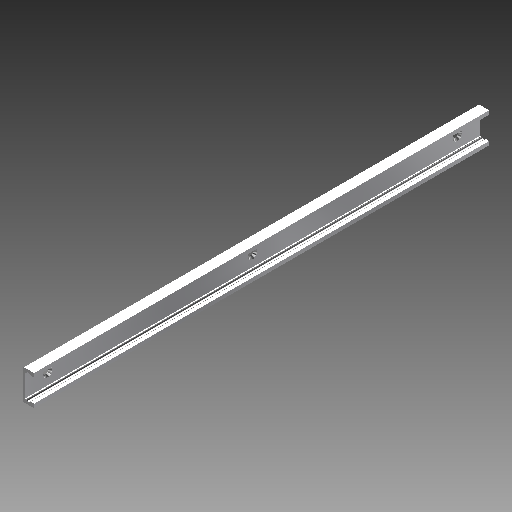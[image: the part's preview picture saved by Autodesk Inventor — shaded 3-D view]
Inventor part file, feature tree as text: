
AUTODESK INVENTOR PART (.ipt)
format: ipt  version: 2019 (Build 230136000, 136)  size: 131,072 bytes
history: native  units: mm
features: other x21, sketch x2, extrude x1, revolve x1, pattern_linear x1
ambient origin geometry x8: Origin, YZ Plane, XZ Plane, XY Plane, X Axis, Y Axis, Z Axis, Center Point
bodies: Solid1 (feature_tree)
feature tree (26):
  extrude  "Extrusion1"  TaperAngle=360.0deg  [1 undecoded]
  revolve  "Revolution1"  [1 undecoded]
  pattern_linear  "Rectangular Pattern1"  [2 undecoded]
  other  "to_ball_XY"
  other  "to_ball_YZ"
  other  "to_ball_ZX"
  other  "to_ball_X"
  other  "to_ball_Y"
  other  "to_ball_Z"
  other  "to_ball_Center"
  other  "to_ball1_XY"
  other  "to_ball1_YZ"
  other  "to_ball1_ZX"
  other  "to_ball1_X"
  other  "to_ball1_Y"
  other  "to_ball1_Z"
  other  "to_ball1_Center"
  other  "to_rail_XY"
  other  "to_rail_YZ"
  other  "to_rail_ZX"
  other  "to_rail_X"
  other  "to_rail_Y"
  other  "to_rail_Z"
  other  "to_rail_Center"
  sketch  "Sketch_1"  dims[d0=300.0mm d1=0.0mm d2=360.0deg]
  sketch  "Sketch_2"  dims[d3=30.0mm d5=135.0mm d6=10.0mm d8=0.0mm]
note: 4 required parameter values undecoded (feature->parameter linkage not recoverable at this tier; creation-order binding heuristic only, values carry confidence <= 0.55)
